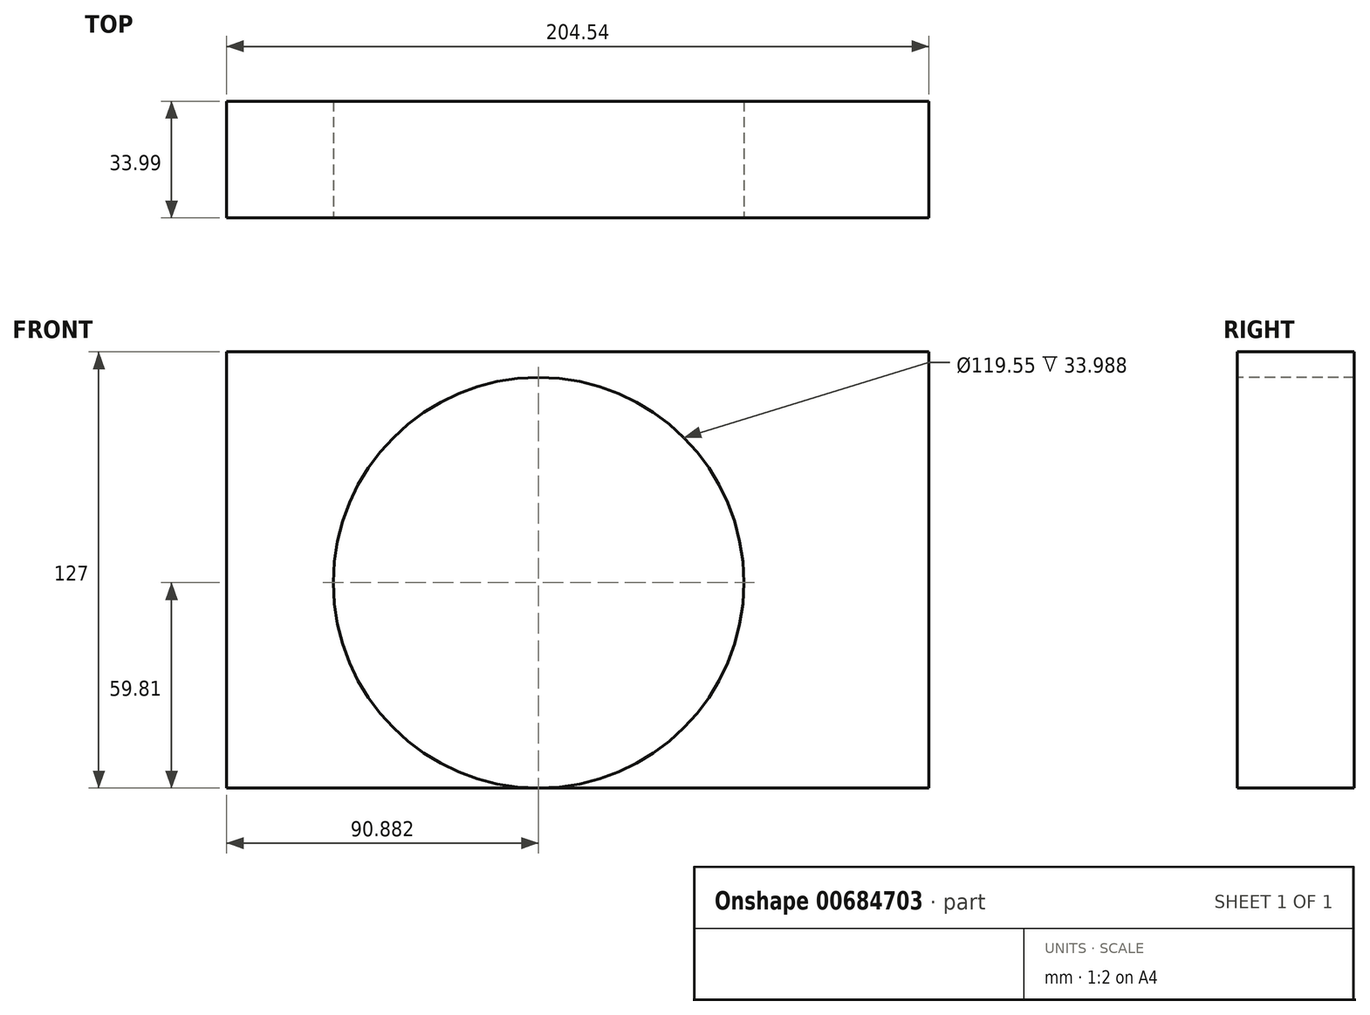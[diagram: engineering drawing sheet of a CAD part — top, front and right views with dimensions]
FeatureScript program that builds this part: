
annotation { "Feature Type Name" : "Feature", "Feature Type Description" : "" }
export const myFeature = defineFeature(function(context is Context, id is Id, definition is map)
    precondition{}
    {
        {
            var Q0;
            Q0=qCreatedBy(makeId("Top.planeOp"),FACE);
            var sketch = newSketch(context, id + "F0", { "sketchPlane" : qUnion([Q0])});
            skLineSegment(sketch, "E0.bottom", {"start": v(-56.16, -55.15) * mm, "end": v(148.38, -55.15) * mm});
            skLineSegment(sketch, "E0.top", {"start": v(-56.16, -21.16) * mm, "end": v(148.38, -21.16) * mm});
            skLineSegment(sketch, "E0.left", {"start": v(-56.16, -55.15) * mm, "end": v(-56.16, -21.16) * mm});
            skLineSegment(sketch, "E0.right", {"start": v(148.38, -55.15) * mm, "end": v(148.38, -21.16) * mm});
            skSolve(sketch);
        }
        {
            var Q0;
            Q0 = qSketchRegion(id + "F0", true);
            extrude(context, id + "F1", {"entities" : qUnion([Q0]), "depth" : 127 * mm, "offsetDistance" : 25.4 * mm});
        }
        {
            var Q0;
            Q0=makeQuery(id+"F1.opExtrude","SWEPT_FACE",FACE,{"disambiguationData":[OSD([sQuery(id+"F0.wireOp",EDGE,"E0.bottom")])]});
            var sketch = newSketch(context, id + "F2", { "sketchPlane" : qUnion([Q0])});
            skCircle(sketch, "E1", {"center": v(34.72, 59.81) * mm, "radius": 59.78 * mm});
            skSolve(sketch);
        }
        {
            var Q0;
            Q0 = qSketchRegion(id + "F2", true);
            extrude(context, id + "F3", {"entities" : qUnion([Q0]), "operationType" : NewBodyOperationType.REMOVE, "endBound" : BoundingType.THROUGH_ALL, "oppositeDirection" : true, "depth" : 25.4 * mm, "offsetDistance" : 25.4 * mm});
        }
    });
